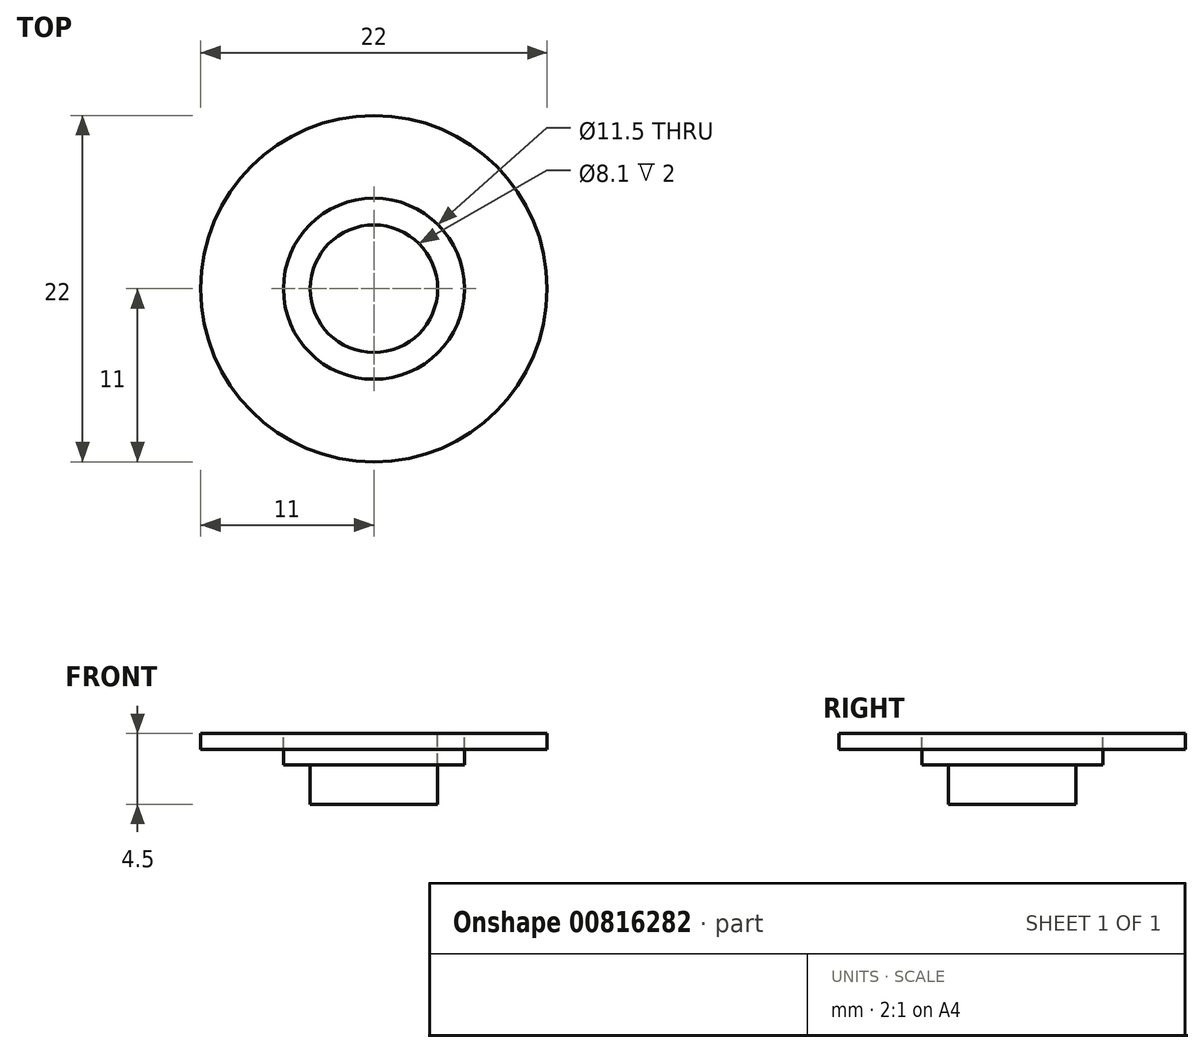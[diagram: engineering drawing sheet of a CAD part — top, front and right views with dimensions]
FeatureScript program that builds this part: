
annotation { "Feature Type Name" : "Feature", "Feature Type Description" : "" }
export const myFeature = defineFeature(function(context is Context, id is Id, definition is map)
    precondition{}
    {
        {
            var Q0;
            Q0=qCreatedBy(makeId("Top.planeOp"),FACE);
            var sketch = newSketch(context, id + "F0", { "sketchPlane" : qUnion([Q0])});
            skCircle(sketch, "E0", {"center": v(0, 0) * mm, "radius": 4.05 * mm});
            skCircle(sketch, "E1", {"center": v(0, 0) * mm, "radius": 5.75 * mm});
            skCircle(sketch, "E2", {"center": v(0, 0) * mm, "radius": 11 * mm});
            skSolve(sketch);
        }
        {
            var Q0;
            Q0=makeQuery(id+"F0.imprint","IMPRINT",FACE,{"disambiguationData":[TD([[makeQuery(id+"F0.imprint","IMPRINT",EDGE,{"derivedFrom":sQuery(id+"F0.wireOp",EDGE,"E0")}),-1.0]])]});
            extrude(context, id + "F1", {"entities" : qUnion([Q0]), "oppositeDirection" : true, "depth" : 2 * mm, "offsetDistance" : 25 * mm});
        }
        {
            var Q0;
            Q0=makeQuery(id+"F0.imprint","IMPRINT",FACE,{"disambiguationData":[TD([[makeQuery(id+"F0.imprint","IMPRINT",EDGE,{"derivedFrom":sQuery(id+"F0.wireOp",EDGE,"E1")}),-1.0]])]});
            extrude(context, id + "F2", {"entities" : qUnion([Q0]), "oppositeDirection" : true, "depth" : 1 * mm, "offsetDistance" : 25 * mm});
        }
        {
            var Q0;
            Q0=makeQuery(id+"F0.imprint","IMPRINT",FACE,{"disambiguationData":[TD([[makeQuery(id+"F0.imprint","IMPRINT",EDGE,{"derivedFrom":sQuery(id+"F0.wireOp",EDGE,"E0")}),1.0]])]});
            extrude(context, id + "F3", {"entities" : qUnion([Q0]), "oppositeDirection" : true, "depth" : 4.5 * mm, "offsetDistance" : 25 * mm});
        }
    });
